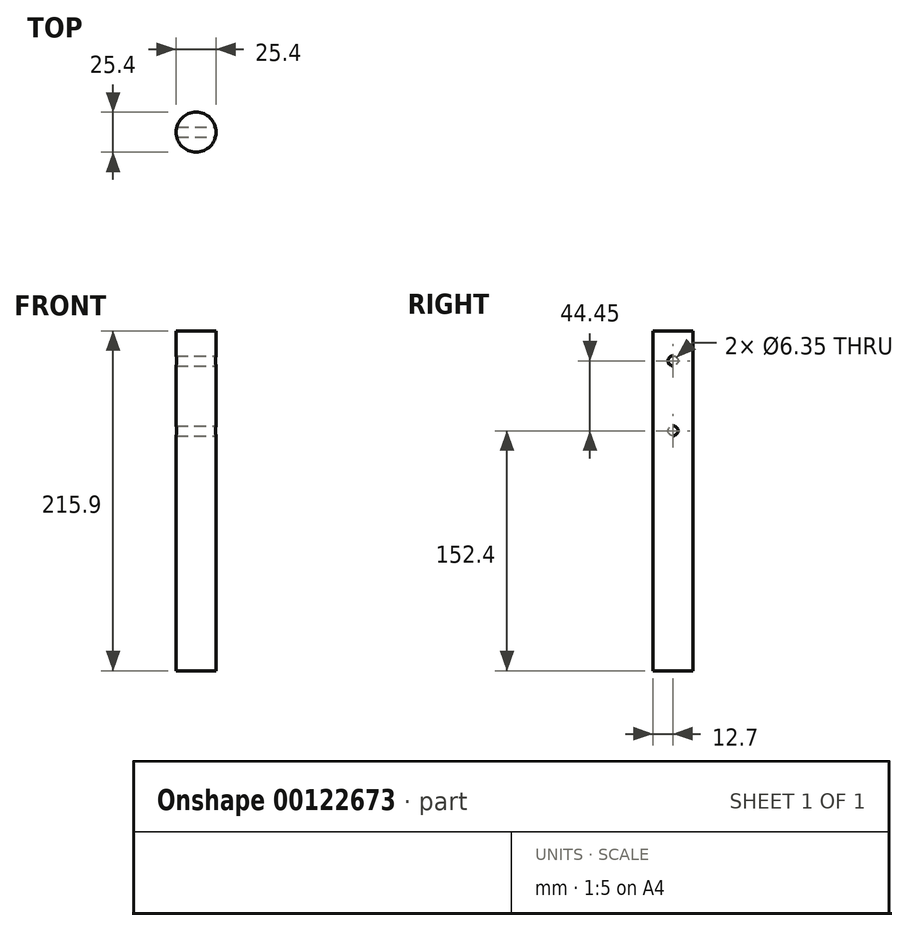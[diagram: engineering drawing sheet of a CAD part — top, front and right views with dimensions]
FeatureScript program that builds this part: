
annotation { "Feature Type Name" : "Feature", "Feature Type Description" : "" }
export const myFeature = defineFeature(function(context is Context, id is Id, definition is map)
    precondition{}
    {
        {
            var Q0;
            Q0=qCreatedBy(makeId("Top.planeOp"),FACE);
            var sketch = newSketch(context, id + "F0", { "sketchPlane" : qUnion([Q0])});
            skCircle(sketch, "E0", {"center": v(0, 0) * mm, "radius": 12.7 * mm});
            skSolve(sketch);
        }
        {
            var Q0;
            Q0=makeQuery(id+"F0.imprint","IMPRINT",FACE,{"disambiguationData":[TD([[makeQuery(id+"F0.imprint","IMPRINT",EDGE,{"derivedFrom":sQuery(id+"F0.wireOp",EDGE,"E0")}),1.0]])]});
            extrude(context, id + "F1", {"entities" : qUnion([Q0]), "oppositeDirection" : true, "depth" : 215.9 * mm});
        }
        {
            var Q0;
            Q0=qCreatedBy(makeId("Right.planeOp"),FACE);
            var sketch = newSketch(context, id + "F2", { "sketchPlane" : qUnion([Q0])});
            skCircle(sketch, "E1", {"center": v(0, -19.05) * mm, "radius": 3.18 * mm});
            skCircle(sketch, "E2", {"center": v(0, -63.5) * mm, "radius": 3.18 * mm});
            skSolve(sketch);
        }
        {
            var Q0;
            Q0 = qSketchRegion(id + "F2", true);
            extrude(context, id + "F3", {"entities" : qUnion([Q0]), "operationType" : NewBodyOperationType.REMOVE, "oppositeDirection" : true, "depth" : 25.4 * mm, "hasSecondDirection" : true, "secondDirectionOppositeDirection" : true, "secondDirectionDepth" : 25.4 * mm, "symmetric" : true});
        }
    });
